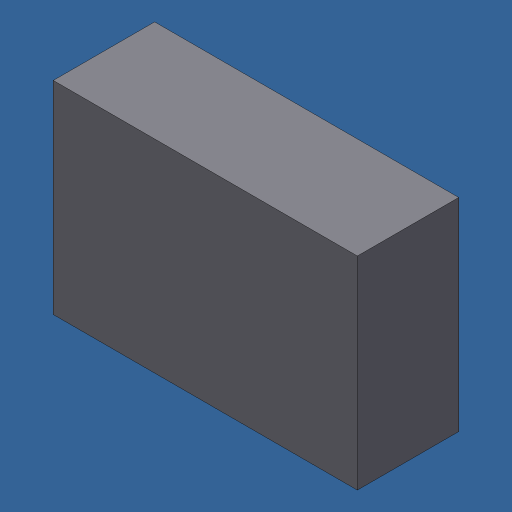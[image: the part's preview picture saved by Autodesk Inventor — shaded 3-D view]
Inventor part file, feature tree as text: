
AUTODESK INVENTOR PART (.ipt)
format: ipt  version: 2024.3 (Build 283343000, 343)  size: 112,128 bytes
history: native  units: mm
features: other x1, extrude x1
ambient origin geometry x8: Origin, YZ Plane, XZ Plane, XY Plane, X Axis, Y Axis, Z Axis, Center Point
bodies: Body1 (feature_tree)
feature tree (2):
  other  "Finish - None"
  extrude  "Extrusion1"  TaperAngle=0.0deg  [1 undecoded]
note: 1 required parameter value undecoded (feature->parameter linkage not recoverable at this tier; creation-order binding heuristic only, values carry confidence <= 0.55)
